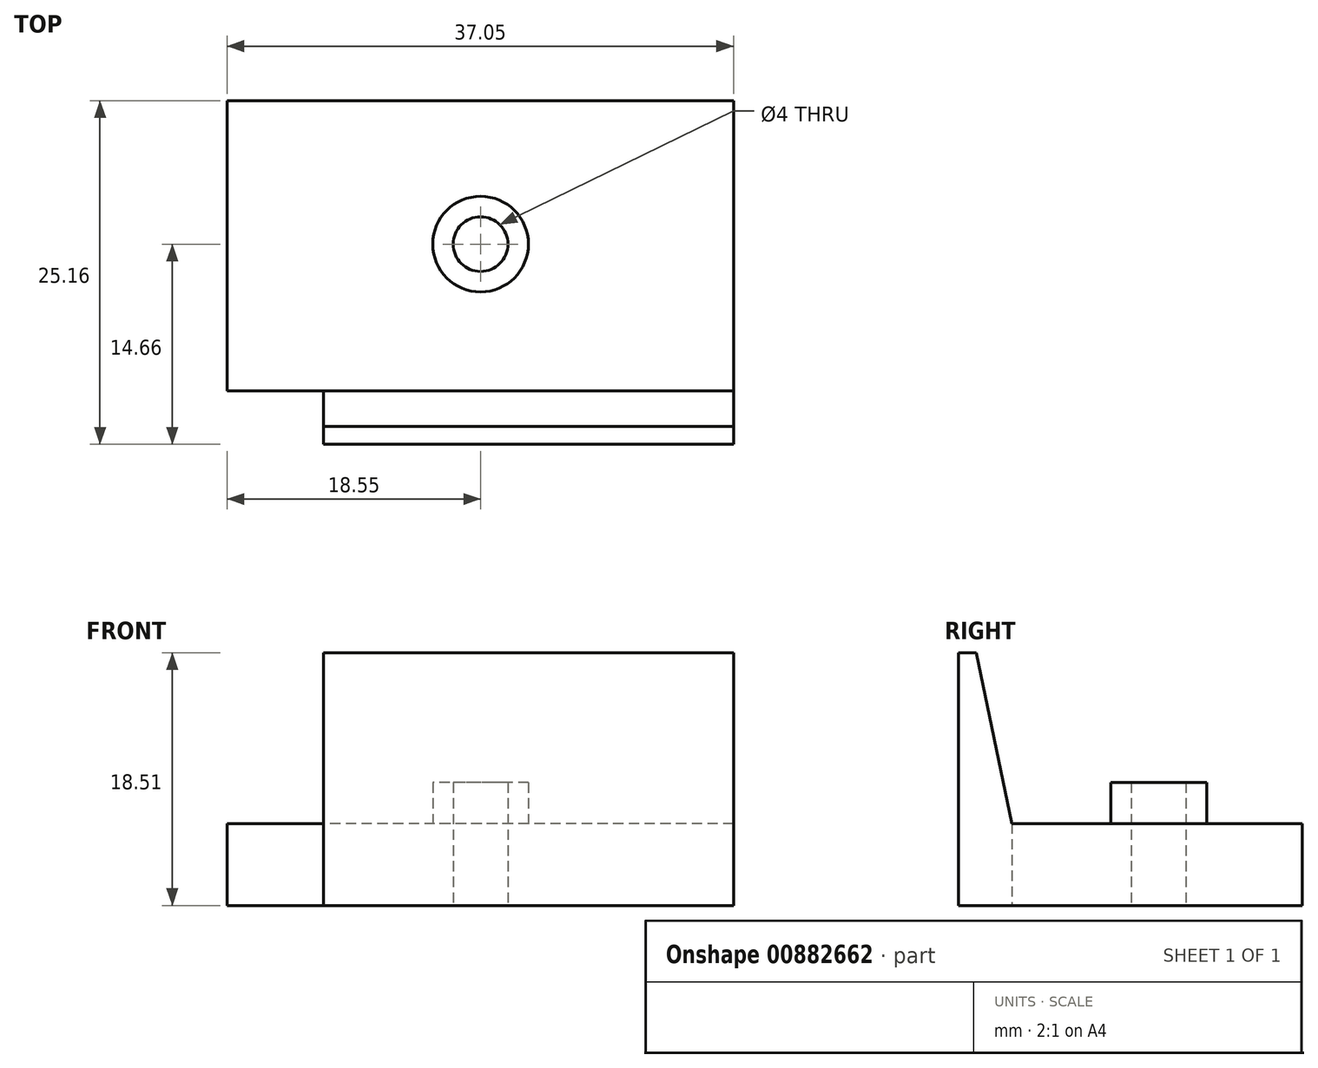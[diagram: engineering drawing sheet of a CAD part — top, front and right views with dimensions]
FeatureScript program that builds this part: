
annotation { "Feature Type Name" : "Feature", "Feature Type Description" : "" }
export const myFeature = defineFeature(function(context is Context, id is Id, definition is map)
    precondition{}
    {
        {
            var Q0;
            Q0=qCreatedBy(makeId("Top.planeOp"),FACE);
            var sketch = newSketch(context, id + "F0", { "sketchPlane" : qUnion([Q0])});
            skLineSegment(sketch, "E0.bottom", {"start": v(0, 0) * mm, "end": v(-37.05, 0) * mm});
            skLineSegment(sketch, "E0.top", {"start": v(0, 21.25) * mm, "end": v(-37.05, 21.25) * mm});
            skLineSegment(sketch, "E0.left", {"start": v(0, 0) * mm, "end": v(0, 21.25) * mm});
            skLineSegment(sketch, "E0.right", {"start": v(-37.05, 0) * mm, "end": v(-37.05, 21.25) * mm});
            skLineSegment(sketch, "E1.bottom", {"start": v(-37.05, 21.25) * mm, "end": v(-33.55, 21.25) * mm});
            skLineSegment(sketch, "E1.top", {"start": v(-37.05, 36.25) * mm, "end": v(-33.55, 36.25) * mm});
            skLineSegment(sketch, "E1.left", {"start": v(-37.05, 21.25) * mm, "end": v(-37.05, 36.25) * mm});
            skLineSegment(sketch, "E1.right", {"start": v(-33.55, 21.25) * mm, "end": v(-33.55, 36.25) * mm});
            skSolve(sketch);
        }
        {
            var Q0;
            Q0=makeQuery(id+"F0.imprint","IMPRINT",FACE,{"disambiguationData":[TD([[makeQuery(id+"F0.imprint","IMPRINT",EDGE,{"derivedFrom":sQuery(id+"F0.wireOp",EDGE,"E1.bottom")}),1.0]])]});
            var Q1;
            Q1=makeQuery(id+"F0.imprint","IMPRINT",FACE,{"disambiguationData":[TD([[makeQuery(id+"F0.imprint","IMPRINT",EDGE,{"derivedFrom":sQuery(id+"F0.wireOp",EDGE,"E0.bottom")}),-1.0]])]});
            extrude(context, id + "F1", {"entities" : qUnion([Q0, Q1]), "depth" : 6 * mm, "offsetDistance" : 25 * mm});
        }
        {
            var Q0;
            Q0=makeQuery(id+"F1.opExtrude","CAP_FACE",FACE,{"disambiguationData":[OSD([sQuery(id+"F0.wireOp",EDGE,"E0.bottom"),sQuery(id+"F0.wireOp",EDGE,"E0.top"),sQuery(id+"F0.wireOp",EDGE,"E0.left"),sQuery(id+"F0.wireOp",EDGE,"E0.right"),sQuery(id+"F0.wireOp",EDGE,"E1.top"),sQuery(id+"F0.wireOp",EDGE,"E1.left"),sQuery(id+"F0.wireOp",EDGE,"E1.right")])],"isStart":false});
            var sketch = newSketch(context, id + "F2", { "sketchPlane" : qUnion([Q0])});
            skCircle(sketch, "E2", {"center": v(-18.5, 10.75) * mm, "radius": 2 * mm});
            skCircle(sketch, "E3", {"center": v(-18.5, 10.75) * mm, "radius": 3.5 * mm});
            skSolve(sketch);
        }
        {
            var Q0;
            Q0=makeQuery(id+"F2.imprint","IMPRINT",FACE,{"disambiguationData":[TD([[makeQuery(id+"F2.imprint","IMPRINT",EDGE,{"derivedFrom":sQuery(id+"F2.wireOp",EDGE,"E2")}),-1.0]])]});
            extrude(context, id + "F3", {"entities" : qUnion([Q0]), "operationType" : NewBodyOperationType.ADD, "depth" : 3 * mm, "offsetDistance" : 25 * mm});
        }
        {
            var Q0;
            Q0=makeQuery(id+"F3.boolean.opBoolean","SPLIT",FACE,{"disambiguationData":[TD([makeQuery(id+"F3.opExtrude","SWEPT_FACE",FACE,{"disambiguationData":[OSD([sQuery(id+"F2.wireOp",EDGE,"E2")])]})])],"derivedFrom":makeQuery(id+"F1.opExtrude","CAP_FACE",FACE,{"disambiguationData":[OSD([sQuery(id+"F0.wireOp",EDGE,"E0.bottom"),sQuery(id+"F0.wireOp",EDGE,"E0.top"),sQuery(id+"F0.wireOp",EDGE,"E0.left"),sQuery(id+"F0.wireOp",EDGE,"E0.right"),sQuery(id+"F0.wireOp",EDGE,"E1.top"),sQuery(id+"F0.wireOp",EDGE,"E1.left"),sQuery(id+"F0.wireOp",EDGE,"E1.right")])],"isStart":false})});
            extrude(context, id + "F4", {"entities" : qUnion([Q0]), "operationType" : NewBodyOperationType.REMOVE, "oppositeDirection" : true, "depth" : 25 * mm, "offsetDistance" : 25 * mm});
        }
        {
            var Q0;
            Q0=makeQuery(id+"F1.opExtrude","SWEPT_FACE",FACE,{"disambiguationData":[OSD([sQuery(id+"F0.wireOp",EDGE,"E0.left")])]});
            var sketch = newSketch(context, id + "F5", { "sketchPlane" : qUnion([Q0])});
            skLineSegment(sketch, "E4", {"start": v(0, 0) * mm, "end": v(-3.91, 0) * mm});
            skLineSegment(sketch, "E5", {"start": v(-3.91, 0) * mm, "end": v(-3.91, 18.5) * mm});
            skLineSegment(sketch, "E6", {"start": v(-3.91, 18.5) * mm, "end": v(-2.61, 18.5) * mm});
            skLineSegment(sketch, "E7", {"start": v(-2.61, 18.5) * mm, "end": v(0, 6) * mm});
            skSolve(sketch);
        }
        {
            var Q0;
            Q0=makeQuery(id+"F5.imprint","IMPRINT",FACE,{"disambiguationData":[TD([[makeQuery(id+"F5.imprint","IMPRINT",EDGE,{"derivedFrom":sQuery(id+"F5.wireOp",EDGE,"E4")}),-1.0]])]});
            extrude(context, id + "F6", {"entities" : qUnion([Q0]), "operationType" : NewBodyOperationType.ADD, "oppositeDirection" : true, "depth" : 30 * mm, "offsetDistance" : 25 * mm});
        }
    });
